# Revit family: 873-00-002-DN200-250
name_source: partatom
category: Pipe Accessories
units: mm (PartAtom-declared; Revit-internal decimal feet)

## family parameters
Always vertical = Yes
Cut with Voids When Loaded = No
Part Type = Valve - Breaks Into
Round Connector Dimension = Use Diameter
Shared = No
Work Plane-Based = No

## types (2) — shared parameters
873-0200-00-741000 = DN200_PN25
873-0250-00-741000 = DN250_PN25
Body_Wallthicknss = 10 mm  [stored 0.0328084 ft]
Description_ = AVK DISMANTLING JOINT
Flange_thickness = 20 mm  [stored 0.0656168 ft]
Search_table = 873-00-002-DN200-250
URL product pages = https://www.avkvalves.com

## per-type parameters (varying)
| type | A | DN | Id(Radius) | L | T | d1 | d2 |
| DN200 | 205 mm  [stored 0.672572 ft] | 200 mm  [stored 0.656168 ft] | 100 mm  [stored 0.328084 ft] | 400 mm  [stored 1.31234 ft] | 24 mm  [stored 0.0787402 ft] | 310 mm  [stored 1.01706 ft] | 180 mm  [stored 0.590551 ft] |
| DN250 | 225 mm  [stored 0.738189 ft] | 250 mm  [stored 0.82021 ft] | 125 mm  [stored 0.410105 ft] | 450 mm  [stored 1.47638 ft] | 27 mm  [stored 0.0885827 ft] | 370 mm  [stored 1.21391 ft] | 213 mm |

note: [stored X ft] marks values corroborated as IEEE doubles in the binary element streams (Revit-internal decimal feet)

## geometry (parser evidence)
native form markers: Sweep x11
no freeform markers — native parametric forms only
